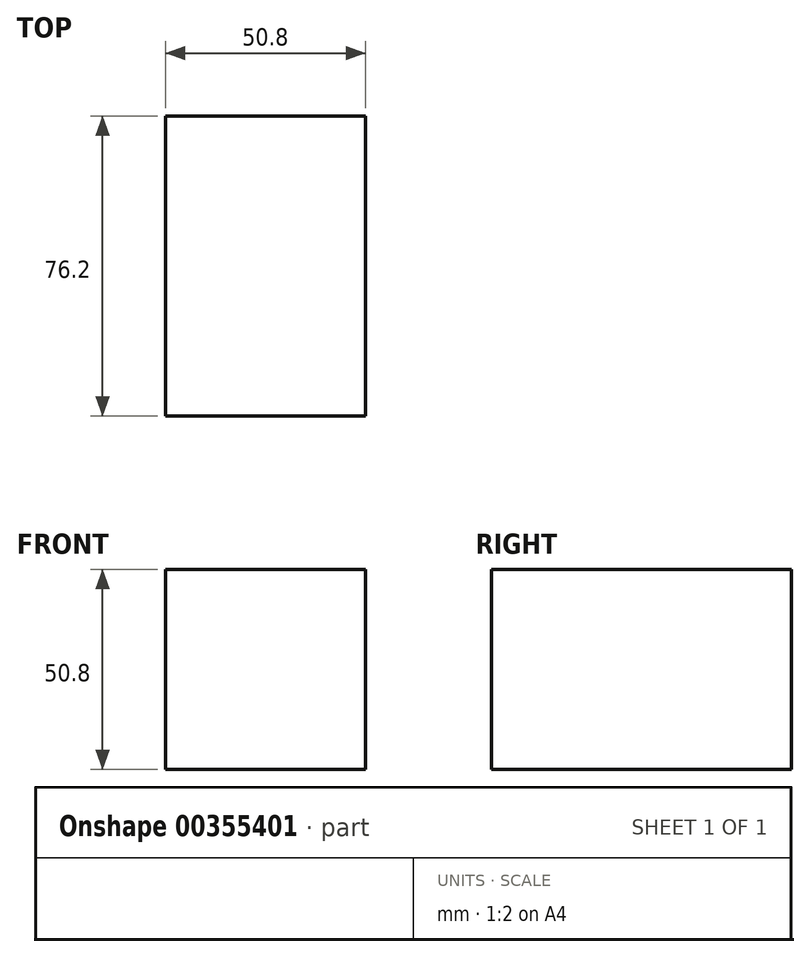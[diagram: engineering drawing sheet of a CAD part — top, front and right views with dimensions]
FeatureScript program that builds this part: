
annotation { "Feature Type Name" : "Feature", "Feature Type Description" : "" }
export const myFeature = defineFeature(function(context is Context, id is Id, definition is map)
    precondition{}
    {
        {
            var Q0;
            Q0=qCreatedBy(makeId("Front.planeOp"),FACE);
            var sketch = newSketch(context, id + "F0", { "sketchPlane" : qUnion([Q0])});
            skLineSegment(sketch, "E0.bottom", {"start": v(0, 0) * mm, "end": v(50.8, 0) * mm});
            skLineSegment(sketch, "E0.top", {"start": v(0, 50.8) * mm, "end": v(50.8, 50.8) * mm});
            skLineSegment(sketch, "E0.left", {"start": v(0, 0) * mm, "end": v(0, 50.8) * mm});
            skLineSegment(sketch, "E0.right", {"start": v(50.8, 0) * mm, "end": v(50.8, 50.8) * mm});
            skSolve(sketch);
        }
        {
            var Q0;
            Q0 = qSketchRegion(id + "F0", true);
            extrude(context, id + "F1", {"entities" : qUnion([Q0]), "depth" : 76.2 * mm});
        }
    });
